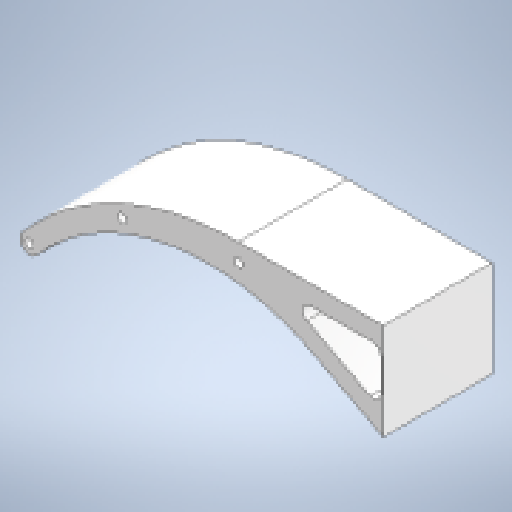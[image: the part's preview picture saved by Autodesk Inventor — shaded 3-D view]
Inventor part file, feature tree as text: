
AUTODESK INVENTOR PART (.ipt)
format: ipt  version: 2025.1 (Build 291241000, 241)  size: 168,448 bytes
history: native  units: mm
features: other x6, reference x2, sketch x1, extrude x1, fillet x1
ambient origin geometry x8: Origin, YZ Plane, XZ Plane, XY Plane, X Axis, Y Axis, Z Axis, Center Point
bodies: Body1 (feature_tree)
feature tree (11):
  other  "ソリッド1"
  sketch  "スケッチ1"
  other  "作業平面1"
  extrude  "押し出し1"  Depth=1.6mm
  fillet  "フィレット1"  Radius=1.6mm
  reference  "参照1"
  reference  "参照2"
  other  "<userpath>\Documents\Inventor\Vixen\doutai.iam"
  other  "doutai.iam"
  other  "tesaki:1"
  other  "KRS3300_scale:1"
